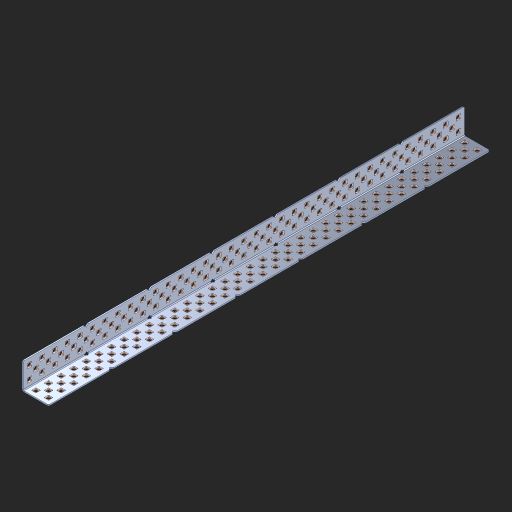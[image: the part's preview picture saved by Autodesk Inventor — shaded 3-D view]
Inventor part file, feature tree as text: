
AUTODESK INVENTOR PART (.ipt)
format: ipt  version: 2023 (Build 270158000, 158)  size: 2,252,800 bytes
history: native  units: in
note: dims shown in document units (in); Inventor stores cm internally (conversion verified against a paired STEP export)
features: other x286, extrude x206, sheet_metal_op x8, sketch x7, pattern_linear x2, mirror x1, chamfer x1
ambient origin geometry x8: Origin, YZ Plane, XZ Plane, XY Plane, X Axis, Y Axis, Z Axis, Center Point
bodies: Solid1 (feature_tree), Body (feature_tree)
feature tree (511):
  other  "Table"
  other  "Alu Angle 2x2x35"
  other  "Alu Angle 2x2x34"
  other  "Alu Angle 2x2x33"
  other  "Alu Angle 2x2x32"
  other  "Alu Angle 2x2x31"
  other  "Alu Angle 2x2x30"
  other  "Alu Angle 2x2x29"
  other  "Alu Angle 2x2x28"
  other  "Alu Angle 2x2x27"
  other  "Alu Angle 2x2x26"
  other  "Alu Angle 2x2x25"
  other  "Alu Angle 2x2x24"
  other  "Alu Angle 2x2x23"
  other  "Alu Angle 2x2x22"
  other  "Alu Angle 2x2x21"
  other  "Alu Angle 2x2x20"
  other  "Alu Angle 2x2x19"
  other  "Alu Angle 2x2x18"
  other  "Alu Angle 2x2x17"
  other  "Alu Angle 2x2x16"
  other  "Alu Angle 2x2x15"
  other  "Alu Angle 2x2x14"
  other  "Alu Angle 2x2x13"
  other  "Alu Angle 2x2x12"
  other  "Alu Angle 2x2x11"
  other  "Alu Angle 2x2x10"
  other  "Alu Angle 2x2x9"
  other  "Alu Angle 2x2x8"
  other  "Alu Angle 2x2x7"
  other  "Alu Angle 2x2x6"
  other  "Alu Angle 2x2x5"
  other  "Alu Angle 2x2x4"
  other  "Alu Angle 2x2x3"
  other  "Alu Angle 2x2x2"
  other  "Alu Angle 2x2x1"
  other  "Steel Angle 2x2x35"
  other  "Steel Angle 2x2x34"
  other  "Steel Angle 2x2x33"
  other  "Steel Angle 2x2x32"
  other  "Steel Angle 2x2x31"
  other  "Steel Angle 2x2x30"
  other  "Steel Angle 2x2x29"
  other  "Steel Angle 2x2x28"
  other  "Steel Angle 2x2x27"
  other  "Steel Angle 2x2x26"
  other  "Steel Angle 2x2x25"
  other  "Steel Angle 2x2x24"
  other  "Steel Angle 2x2x23"
  other  "Steel Angle 2x2x22"
  other  "Steel Angle 2x2x21"
  other  "Steel Angle 2x2x20"
  other  "Steel Angle 2x2x19"
  other  "Steel Angle 2x2x18"
  other  "Steel Angle 2x2x17"
  other  "Steel Angle 2x2x16"
  other  "Steel Angle 2x2x15"
  other  "Steel Angle 2x2x14"
  other  "Steel Angle 2x2x13"
  other  "Steel Angle 2x2x12"
  other  "Steel Angle 2x2x11"
  other  "Steel Angle 2x2x10"
  other  "Steel Angle 2x2x9"
  other  "Steel Angle 2x2x8"
  other  "Steel Angle 2x2x7"
  other  "Steel Angle 2x2x6"
  other  "Steel Angle 2x2x5"
  other  "Steel Angle 2x2x4"
  other  "Steel Angle 2x2x3"
  other  "Steel Angle 2x2x2"
  other  "Steel Angle 2x2x1"
  other  "Steel Angle 3x3x35"
  sheet_metal_op  "Flanges"
  sheet_metal_op  "Body Pattern"
  pattern_linear  "Center Pattern"  Spacing1=1.0in  [1 undecoded]
  other  "Arc Length"
  pattern_linear  "Notch Pattern"  Spacing1=0.1875in  [1 undecoded]
  other  "Diagonal Plane"
  mirror  "Everything Mirrored"
  chamfer  "End Chamfer"
  sketch  "Sketch1"  dims[d0=1.0in]
  other  "Plate1"
  sketch  "Sketch2"  dims[d1=17.5in]
  other  "Plate2"
  sheet_metal_op  "Bend1"
  sheet_metal_op  "Corner1"
  sketch  "Sketch8"  dims[d2=0.0469in]
  sketch  "Sketch9"  dims[d3=0.0469in]
  other  "Srf91"
  sheet_metal_op  "Body Pattern Sketch"
  other  "Srf92"
  sketch  "Sketch13"  dims[d4=0.0234in]
  sketch  "Sketch15"  dims[d5=0.0938in]
  sketch  "Sketch16"  dims[d6=0.0469in d7=1.0in d8=90.0deg d9=0.0312in d10=0.1875in d11=0.0469in d12=0.0469in d49=0.182in d50=0.02in d52=0.25in d53=0.0469in d54=0.0in d55=0.172in d56=1.0in d57=0.0in d60=13.7795in d62=0.5in d63=0.7874in d65=0.5in d85=0.1473in d86=0.1659in d89=0.0469in d90=0.0in d91=0.04in d92=0.0491in d95=2.5in d96=0.04in d97=0.25in d98=45.0deg d99=0.25in d106=0.182in d107=0.02in d108=0.5in d110=0.0469in d111=0.0in d112=0.172in d113=0.5in d114=0.0in d117=0.5in d123=0.25in d125=0.25in d126=0.0491in d127=0.1227in d128=0.08in d129=0.04in d130=2.5in]
  other  "Srf786"
  other  "Srf856"
  other  "Srf857"
  other  "Srf858"
  other  "Srf859"
  other  "Srf860"
  other  "Srf861"
  other  "Srf889"
  other  "Srf890"
  other  "Srf891"
  other  "Srf1275"
  other  "Srf1276"
  other  "Srf1278"
  other  "Srf1279"
  other  "Srf1280"
  other  "Srf1281"
  other  "Srf1282"
  other  "Srf1283"
  other  "Srf1277"
  other  "Srf1285"
  other  "Srf1286"
  other  "Srf1287"
  other  "Srf1383"
  other  "Srf1384"
  other  "Srf1385"
  other  "Srf1386"
  other  "Srf1387"
  other  "Srf1388"
  other  "Srf1389"
  other  "Srf1390"
  other  "Srf1391"
  other  "Srf1392"
  other  "Srf1393"
  other  "Srf1394"
  other  "Srf1395"
  other  "Srf1396"
  other  "Srf1397"
  other  "Srf1398"
  other  "Srf1399"
  other  "Srf1400"
  other  "Srf1401"
  other  "Srf1402"
  other  "Srf1403"
  other  "Srf1404"
  other  "Srf1405"
  other  "Srf1406"
  other  "Srf1407"
  other  "Srf1408"
  other  "Srf1409"
  other  "Srf1410"
  other  "Srf1411"
  other  "Srf1412"
  other  "Srf1413"
  other  "Srf1414"
  other  "Srf1415"
  other  "Srf1416"
  other  "Srf1417"
  other  "Srf1418"
  other  "Srf1419"
  other  "Srf1420"
  other  "Srf1421"
  other  "Srf1422"
  other  "Srf1423"
  other  "Srf1424"
  other  "Srf1425"
  other  "Srf1426"
  other  "Srf1427"
  other  "Srf1428"
  other  "Srf1429"
  other  "Srf1430"
  other  "Srf1431"
  other  "Srf1432"
  other  "Srf1433"
  other  "Srf1434"
  other  "Srf1435"
  other  "Srf1436"
  other  "Srf1437"
  other  "Srf1438"
  other  "Srf1439"
  other  "Srf1440"
  other  "Srf1441"
  other  "Srf1442"
  other  "Srf1443"
  other  "Srf1444"
  other  "Srf1445"
  other  "Srf1446"
  other  "Srf1447"
  other  "Srf1448"
  other  "Srf1449"
  other  "Srf1450"
  other  "Srf1451"
  other  "Srf1452"
  other  "Srf1453"
  other  "Srf1454"
  other  "Srf1455"
  other  "Srf1456"
  other  "Srf1457"
  other  "Srf1458"
  other  "Srf1459"
  other  "Srf1460"
  other  "Srf1461"
  other  "Srf1462"
  other  "Srf1463"
  other  "Srf1464"
  other  "Srf1465"
  other  "Srf1466"
  other  "Srf1467"
  other  "Srf1468"
  other  "Srf1469"
  other  "Srf1470"
  other  "Srf1471"
  other  "Srf1472"
  other  "Srf1473"
  other  "Srf1474"
  other  "Srf1475"
  other  "Srf1476"
  other  "Srf1477"
  other  "Srf1478"
  other  "Srf1479"
  other  "Srf1480"
  other  "Srf1481"
  other  "Srf1482"
  other  "Srf1483"
  other  "Srf1484"
  other  "Srf1485"
  other  "Srf1486"
  other  "Srf1487"
  other  "Srf1488"
  other  "Srf1489"
  other  "Srf1490"
  other  "Srf1491"
  other  "Srf1492"
  other  "Srf1493"
  other  "Srf1494"
  other  "Srf1495"
  other  "Srf1496"
  other  "Srf1497"
  other  "Srf1498"
  other  "Srf1499"
  other  "Srf1500"
  other  "Srf1501"
  other  "Srf1502"
  other  "Srf1503"
  other  "Srf1504"
  other  "Srf1505"
  other  "Srf1506"
  other  "Srf1507"
  other  "Srf1508"
  other  "Srf1509"
  other  "Srf1510"
  other  "Srf1511"
  other  "Srf1512"
  other  "Srf1513"
  other  "Srf1514"
  other  "Srf1515"
  other  "Srf1516"
  other  "Srf1517"
  other  "Srf1518"
  other  "Srf1519"
  other  "Srf1520"
  other  "Srf1521"
  other  "Srf1522"
  other  "Srf1523"
  other  "Srf1524"
  other  "Srf1525"
  other  "Srf1526"
  other  "Srf1527"
  other  "Srf1528"
  other  "Srf1529"
  other  "Srf1530"
  other  "Srf1531"
  other  "Srf1532"
  other  "Srf1533"
  other  "Srf1534"
  other  "Srf1535"
  other  "Srf1536"
  other  "Srf1537"
  other  "Srf1538"
  other  "Srf1539"
  other  "Srf1540"
  other  "Srf1541"
  other  "Srf1542"
  other  "Srf1543"
  other  "Srf1544"
  other  "Srf1545"
  other  "Srf1546"
  other  "Srf1547"
  other  "Srf1548"
  other  "Srf1549"
  other  "Srf1550"
  other  "Srf1551"
  other  "Srf1552"
  other  "Srf1553"
  other  "Srf1554"
  other  "Srf1555"
  other  "Srf1556"
  other  "Srf1557"
  other  "Srf1558"
  other  "Srf1559"
  other  "Srf1560"
  other  "Srf1561"
  other  "Srf1562"
  other  "Srf1563"
  other  "Srf1564"
  other  "Srf1565"
  other  "Srf1566"
  sheet_metal_op  "Body Stamp"
  sheet_metal_op  "Body Circle"
  other  "Center Stamp"
  other  "Center Circle"
  sheet_metal_op  "Notch"
  extrude  "ExtrusionSrf92"  Depth=0.0469in
  extrude  "ExtrusionSrf856"  Depth=0.0469in
  extrude  "ExtrusionSrf857"  Depth=2.5in
  extrude  "ExtrusionSrf858"  Depth=0.02in
  extrude  "ExtrusionSrf859"  Depth=2.5in
  extrude  "ExtrusionSrf860"  Depth=0.0469in
  extrude  "ExtrusionSrf861"  TaperAngle=0.0deg  [1 undecoded]
  extrude  "ExtrusionSrf889"  Depth=2.5in
  extrude  "ExtrusionSrf890"  Depth=1.0in TaperAngle=0.0deg
  extrude  "ExtrusionSrf891"  Depth=2.5in
  extrude  "ExtrusionSrf1275"  Depth=0.5in
  extrude  "ExtrusionSrf1276"  Depth=2.5in
  extrude  "ExtrusionSrf1277"  Depth=2.5in
  extrude  "ExtrusionSrf1278"  Depth=0.0469in
  extrude  "ExtrusionSrf1279"  Depth=2.5in TaperAngle=0.0deg
  extrude  "ExtrusionSrf1280"  Depth=2.5in
  extrude  "ExtrusionSrf1281"  Depth=2.5in TaperAngle=45.0deg
  extrude  "ExtrusionSrf1282"  Depth=2.5in
  extrude  "ExtrusionSrf1345"  Depth=2.5in
  extrude  "ExtrusionSrf1346"  Depth=0.02in
  extrude  "ExtrusionSrf1347"  Depth=0.5in
  extrude  "ExtrusionSrf1348"  Depth=0.0469in
  extrude  "ExtrusionSrf1383"  TaperAngle=0.0deg  [1 undecoded]
  extrude  "ExtrusionSrf1384"  Depth=2.5in
  extrude  "ExtrusionSrf1385"  Depth=0.5in TaperAngle=0.0deg
  extrude  "ExtrusionSrf1386"  Depth=0.5in
  extrude  "ExtrusionSrf1387"  Depth=2.5in
  extrude  "ExtrusionSrf1388"  Depth=2.5in
  extrude  "ExtrusionSrf1389"  Depth=2.5in
  extrude  "ExtrusionSrf1390"  Depth=2.5in
  extrude  "ExtrusionSrf1391"  Depth=2.5in
  extrude  "ExtrusionSrf1392"  Depth=2.5in
  extrude  "ExtrusionSrf1393"  Depth=2.5in
  extrude  "ExtrusionSrf1394"  [1 undecoded]
  extrude  "ExtrusionSrf1395"  [1 undecoded]
  extrude  "ExtrusionSrf1396"  [1 undecoded]
  extrude  "ExtrusionSrf1397"  [1 undecoded]
  extrude  "ExtrusionSrf1398"  [1 undecoded]
  extrude  "ExtrusionSrf1399"  [1 undecoded]
  extrude  "ExtrusionSrf1400"  [1 undecoded]
  extrude  "ExtrusionSrf1401"  [1 undecoded]
  extrude  "ExtrusionSrf1402"  [1 undecoded]
  extrude  "ExtrusionSrf1403"  [1 undecoded]
  extrude  "ExtrusionSrf1404"  [1 undecoded]
  extrude  "ExtrusionSrf1405"  [1 undecoded]
  extrude  "ExtrusionSrf1406"  [1 undecoded]
  extrude  "ExtrusionSrf1407"  [1 undecoded]
  extrude  "ExtrusionSrf1408"  [1 undecoded]
  extrude  "ExtrusionSrf1409"  [1 undecoded]
  extrude  "ExtrusionSrf1410"  [1 undecoded]
  extrude  "ExtrusionSrf1411"  [1 undecoded]
  extrude  "ExtrusionSrf1412"  [1 undecoded]
  extrude  "ExtrusionSrf1413"  [1 undecoded]
  extrude  "ExtrusionSrf1414"  [1 undecoded]
  extrude  "ExtrusionSrf1415"  [1 undecoded]
  extrude  "ExtrusionSrf1416"  [1 undecoded]
  extrude  "ExtrusionSrf1417"  [1 undecoded]
  extrude  "ExtrusionSrf1418"  [1 undecoded]
  extrude  "ExtrusionSrf1419"  [1 undecoded]
  extrude  "ExtrusionSrf1420"  [1 undecoded]
  extrude  "ExtrusionSrf1421"  [1 undecoded]
  extrude  "ExtrusionSrf1422"  [1 undecoded]
  extrude  "ExtrusionSrf1423"  [1 undecoded]
  extrude  "ExtrusionSrf1424"  [1 undecoded]
  extrude  "ExtrusionSrf1425"  [1 undecoded]
  extrude  "ExtrusionSrf1426"  [1 undecoded]
  extrude  "ExtrusionSrf1427"  [1 undecoded]
  extrude  "ExtrusionSrf1428"  [1 undecoded]
  extrude  "ExtrusionSrf1429"  [1 undecoded]
  extrude  "ExtrusionSrf1430"  [1 undecoded]
  extrude  "ExtrusionSrf1431"  [1 undecoded]
  extrude  "ExtrusionSrf1432"  [1 undecoded]
  extrude  "ExtrusionSrf1433"  [1 undecoded]
  extrude  "ExtrusionSrf1434"  [1 undecoded]
  extrude  "ExtrusionSrf1435"  [1 undecoded]
  extrude  "ExtrusionSrf1436"  [1 undecoded]
  extrude  "ExtrusionSrf1437"  [1 undecoded]
  extrude  "ExtrusionSrf1438"  [1 undecoded]
  extrude  "ExtrusionSrf1439"  [1 undecoded]
  extrude  "ExtrusionSrf1440"  [1 undecoded]
  extrude  "ExtrusionSrf1441"  [1 undecoded]
  extrude  "ExtrusionSrf1442"  [1 undecoded]
  extrude  "ExtrusionSrf1443"  [1 undecoded]
  extrude  "ExtrusionSrf1444"  [1 undecoded]
  extrude  "ExtrusionSrf1445"  [1 undecoded]
  extrude  "ExtrusionSrf1446"  [1 undecoded]
  extrude  "ExtrusionSrf1447"  [1 undecoded]
  extrude  "ExtrusionSrf1448"  [1 undecoded]
  extrude  "ExtrusionSrf1449"  [1 undecoded]
  extrude  "ExtrusionSrf1450"  [1 undecoded]
  extrude  "ExtrusionSrf1451"  [1 undecoded]
  extrude  "ExtrusionSrf1452"  [1 undecoded]
  extrude  "ExtrusionSrf1453"  [1 undecoded]
  extrude  "ExtrusionSrf1454"  [1 undecoded]
  extrude  "ExtrusionSrf1455"  [1 undecoded]
  extrude  "ExtrusionSrf1456"  [1 undecoded]
  extrude  "ExtrusionSrf1457"  [1 undecoded]
  extrude  "ExtrusionSrf1458"  [1 undecoded]
  extrude  "ExtrusionSrf1459"  [1 undecoded]
  extrude  "ExtrusionSrf1460"  [1 undecoded]
  extrude  "ExtrusionSrf1461"  [1 undecoded]
  extrude  "ExtrusionSrf1462"  [1 undecoded]
  extrude  "ExtrusionSrf1463"  [1 undecoded]
  extrude  "ExtrusionSrf1464"  [1 undecoded]
  extrude  "ExtrusionSrf1465"  [1 undecoded]
  extrude  "ExtrusionSrf1466"  [1 undecoded]
  extrude  "ExtrusionSrf1467"  [1 undecoded]
  extrude  "ExtrusionSrf1468"  [1 undecoded]
  extrude  "ExtrusionSrf1469"  [1 undecoded]
  extrude  "ExtrusionSrf1470"  [1 undecoded]
  extrude  "ExtrusionSrf1471"  [1 undecoded]
  extrude  "ExtrusionSrf1472"  [1 undecoded]
  extrude  "ExtrusionSrf1473"  [1 undecoded]
  extrude  "ExtrusionSrf1474"  [1 undecoded]
  extrude  "ExtrusionSrf1475"  [1 undecoded]
  extrude  "ExtrusionSrf1476"  [1 undecoded]
  extrude  "ExtrusionSrf1477"  [1 undecoded]
  extrude  "ExtrusionSrf1478"  [1 undecoded]
  extrude  "ExtrusionSrf1479"  [1 undecoded]
  extrude  "ExtrusionSrf1480"  [1 undecoded]
  extrude  "ExtrusionSrf1481"  [1 undecoded]
  extrude  "ExtrusionSrf1482"  [1 undecoded]
  extrude  "ExtrusionSrf1483"  [1 undecoded]
  extrude  "ExtrusionSrf1484"  [1 undecoded]
  extrude  "ExtrusionSrf1485"  [1 undecoded]
  extrude  "ExtrusionSrf1486"  [1 undecoded]
  extrude  "ExtrusionSrf1487"  [1 undecoded]
  extrude  "ExtrusionSrf1488"  [1 undecoded]
  extrude  "ExtrusionSrf1489"  [1 undecoded]
  extrude  "ExtrusionSrf1490"  [1 undecoded]
  extrude  "ExtrusionSrf1491"  [1 undecoded]
  extrude  "ExtrusionSrf1492"  [1 undecoded]
  extrude  "ExtrusionSrf1493"  [1 undecoded]
  extrude  "ExtrusionSrf1494"  [1 undecoded]
  extrude  "ExtrusionSrf1495"  [1 undecoded]
  extrude  "ExtrusionSrf1496"  [1 undecoded]
  extrude  "ExtrusionSrf1497"  [1 undecoded]
  extrude  "ExtrusionSrf1498"  [1 undecoded]
  extrude  "ExtrusionSrf1499"  [1 undecoded]
  extrude  "ExtrusionSrf1500"  [1 undecoded]
  extrude  "ExtrusionSrf1501"  [1 undecoded]
  extrude  "ExtrusionSrf1502"  [1 undecoded]
  extrude  "ExtrusionSrf1503"  [1 undecoded]
  extrude  "ExtrusionSrf1504"  [1 undecoded]
  extrude  "ExtrusionSrf1505"  [1 undecoded]
  extrude  "ExtrusionSrf1506"  [1 undecoded]
  extrude  "ExtrusionSrf1507"  [1 undecoded]
  extrude  "ExtrusionSrf1508"  [1 undecoded]
  extrude  "ExtrusionSrf1509"  [1 undecoded]
  extrude  "ExtrusionSrf1510"  [1 undecoded]
  extrude  "ExtrusionSrf1511"  [1 undecoded]
  extrude  "ExtrusionSrf1512"  [1 undecoded]
  extrude  "ExtrusionSrf1513"  [1 undecoded]
  extrude  "ExtrusionSrf1514"  [1 undecoded]
  extrude  "ExtrusionSrf1515"  [1 undecoded]
  extrude  "ExtrusionSrf1516"  [1 undecoded]
  extrude  "ExtrusionSrf1517"  [1 undecoded]
  extrude  "ExtrusionSrf1518"  [1 undecoded]
  extrude  "ExtrusionSrf1519"  [1 undecoded]
  extrude  "ExtrusionSrf1520"  [1 undecoded]
  extrude  "ExtrusionSrf1521"  [1 undecoded]
  extrude  "ExtrusionSrf1522"  [1 undecoded]
  extrude  "ExtrusionSrf1523"  [1 undecoded]
  extrude  "ExtrusionSrf1524"  [1 undecoded]
  extrude  "ExtrusionSrf1525"  [1 undecoded]
  extrude  "ExtrusionSrf1526"  [1 undecoded]
  extrude  "ExtrusionSrf1527"  [1 undecoded]
  extrude  "ExtrusionSrf1528"  [1 undecoded]
  extrude  "ExtrusionSrf1529"  [1 undecoded]
  extrude  "ExtrusionSrf1530"  [1 undecoded]
  extrude  "ExtrusionSrf1531"  [1 undecoded]
  extrude  "ExtrusionSrf1532"  [1 undecoded]
  extrude  "ExtrusionSrf1533"  [1 undecoded]
  extrude  "ExtrusionSrf1534"  [1 undecoded]
  extrude  "ExtrusionSrf1535"  [1 undecoded]
  extrude  "ExtrusionSrf1536"  [1 undecoded]
  extrude  "ExtrusionSrf1537"  [1 undecoded]
  extrude  "ExtrusionSrf1538"  [1 undecoded]
  extrude  "ExtrusionSrf1539"  [1 undecoded]
  extrude  "ExtrusionSrf1540"  [1 undecoded]
  extrude  "ExtrusionSrf1541"  [1 undecoded]
  extrude  "ExtrusionSrf1542"  [1 undecoded]
  extrude  "ExtrusionSrf1543"  [1 undecoded]
  extrude  "ExtrusionSrf1544"  [1 undecoded]
  extrude  "ExtrusionSrf1545"  [1 undecoded]
  extrude  "ExtrusionSrf1546"  [1 undecoded]
  extrude  "ExtrusionSrf1547"  [1 undecoded]
  extrude  "ExtrusionSrf1548"  [1 undecoded]
  extrude  "ExtrusionSrf1549"  [1 undecoded]
  extrude  "ExtrusionSrf1550"  [1 undecoded]
  extrude  "ExtrusionSrf1551"  [1 undecoded]
  extrude  "ExtrusionSrf1552"  [1 undecoded]
  extrude  "ExtrusionSrf1553"  [1 undecoded]
  extrude  "ExtrusionSrf1554"  [1 undecoded]
  extrude  "ExtrusionSrf1555"  [1 undecoded]
  extrude  "ExtrusionSrf1556"  [1 undecoded]
  extrude  "ExtrusionSrf1557"  [1 undecoded]
  extrude  "ExtrusionSrf1558"  [1 undecoded]
  extrude  "ExtrusionSrf1559"  [1 undecoded]
  extrude  "ExtrusionSrf1560"  [1 undecoded]
  extrude  "ExtrusionSrf1561"  [1 undecoded]
  extrude  "ExtrusionSrf1562"  [1 undecoded]
  extrude  "ExtrusionSrf1563"  [1 undecoded]
  extrude  "ExtrusionSrf1564"  [1 undecoded]
  extrude  "ExtrusionSrf1565"  [1 undecoded]
  extrude  "ExtrusionSrf1566"  [1 undecoded]
note: 177 required parameter values undecoded (feature->parameter linkage not recoverable at this tier; creation-order binding heuristic only, values carry confidence <= 0.55)
